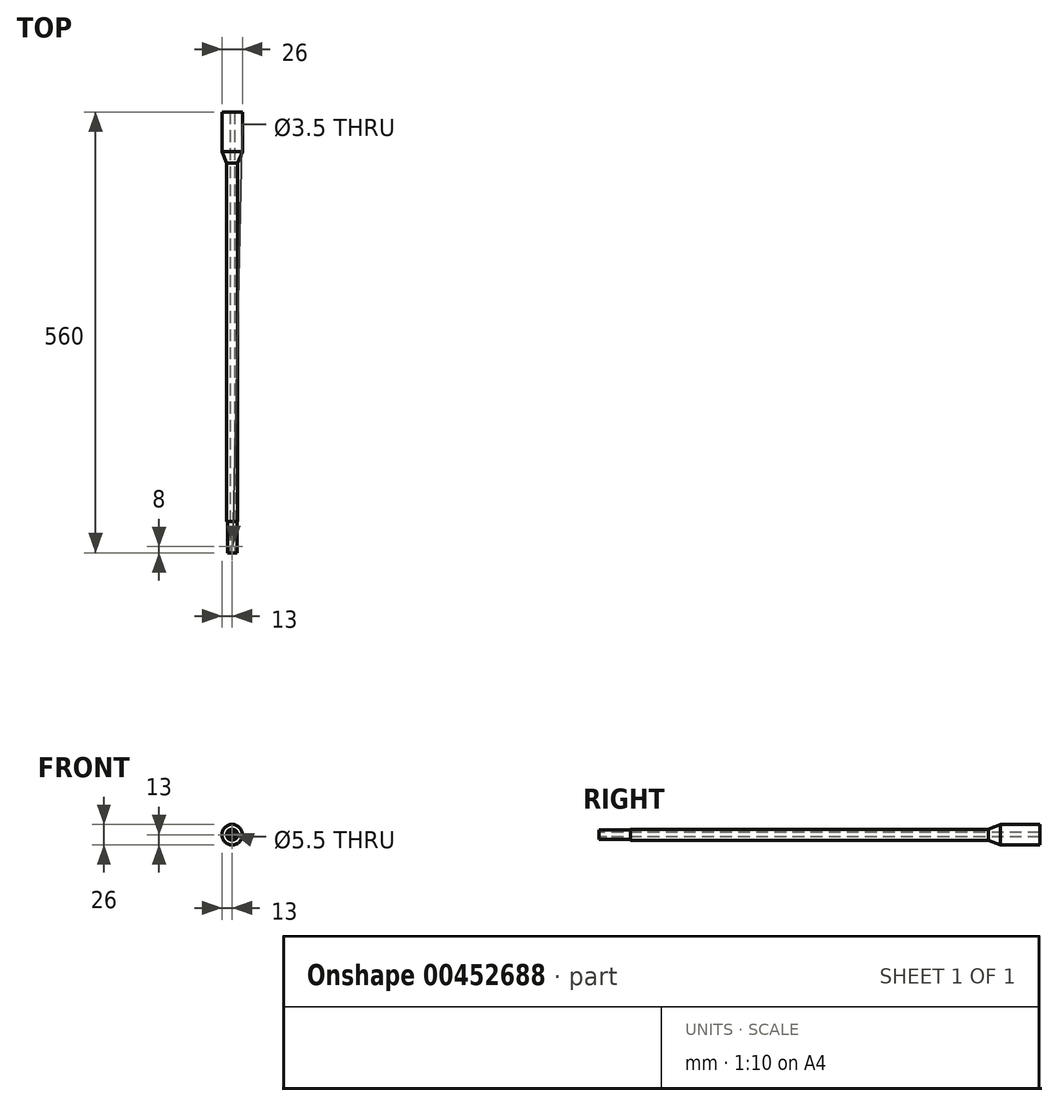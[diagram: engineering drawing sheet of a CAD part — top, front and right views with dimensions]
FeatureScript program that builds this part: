
annotation { "Feature Type Name" : "Feature", "Feature Type Description" : "" }
export const myFeature = defineFeature(function(context is Context, id is Id, definition is map)
    precondition{}
    {
        {
            var Q0;
            Q0=qCreatedBy(makeId("Front.planeOp"),FACE);
            var sketch = newSketch(context, id + "F0", { "sketchPlane" : qUnion([Q0])});
            skCircle(sketch, "E0", {"center": v(0, 0) * mm, "radius": 7 * mm});
            skSolve(sketch);
        }
        {
            var Q0;
            Q0=makeQuery(id+"F0.imprint","IMPRINT",FACE,{"disambiguationData":[TD([[makeQuery(id+"F0.imprint","IMPRINT",EDGE,{"derivedFrom":sQuery(id+"F0.wireOp",EDGE,"E0")}),1.0]])]});
            extrude(context, id + "F1", {"entities" : qUnion([Q0]), "oppositeDirection" : true, "depth" : 560 * mm});
        }
        {
            var Q0;
            Q0=makeQuery(id+"F1.opExtrude","CAP_FACE",FACE,{"disambiguationData":[OSD([sQuery(id+"F0.wireOp",EDGE,"E0")])],"isStart":true});
            var sketch = newSketch(context, id + "F2", { "sketchPlane" : qUnion([Q0])});
            skCircle(sketch, "E1", {"center": v(0, 0) * mm, "radius": 6 * mm});
            skSolve(sketch);
        }
        {
            var Q0;
            Q0=makeQuery(id+"F2.imprint","IMPRINT",FACE,{"disambiguationData":[TD([[makeQuery(id+"F2.imprint","IMPRINT",EDGE,{"derivedFrom":sQuery(id+"F2.wireOp",EDGE,"E1")}),-1.0]])]});
            extrude(context, id + "F3", {"entities" : qUnion([Q0]), "operationType" : NewBodyOperationType.REMOVE, "oppositeDirection" : true, "depth" : 40 * mm});
        }
        {
            var Q0;
            Q0=makeQuery(id+"F1.opExtrude","CAP_FACE",FACE,{"disambiguationData":[OSD([sQuery(id+"F0.wireOp",EDGE,"E0")])],"isStart":true});
            var sketch = newSketch(context, id + "F4", { "sketchPlane" : qUnion([Q0])});
            skCircle(sketch, "E2", {"center": v(0, 0) * mm, "radius": 2.75 * mm});
            skSolve(sketch);
        }
        {
            var Q0;
            Q0=makeQuery(id+"F4.imprint","IMPRINT",FACE,{"disambiguationData":[TD([[makeQuery(id+"F4.imprint","IMPRINT",EDGE,{"derivedFrom":sQuery(id+"F4.wireOp",EDGE,"E2")}),1.0]])]});
            extrude(context, id + "F5", {"entities" : qUnion([Q0]), "operationType" : NewBodyOperationType.REMOVE, "endBound" : BoundingType.THROUGH_ALL, "oppositeDirection" : true, "depth" : 25 * mm});
        }
        {
            var Q0;
            Q0=qCreatedBy(makeId("Top.planeOp"),FACE);
            var sketch = newSketch(context, id + "F6", { "sketchPlane" : qUnion([Q0])});
            skCircle(sketch, "E3", {"center": v(0, 8) * mm, "radius": 1.75 * mm});
            skSolve(sketch);
        }
        {
            var Q0;
            Q0 = qSketchRegion(id + "F6", true);
            extrude(context, id + "F7", {"entities" : qUnion([Q0]), "operationType" : NewBodyOperationType.REMOVE, "oppositeDirection" : true, "depth" : 10 * mm});
        }
        {
            var Q0;
            Q0=makeQuery(id+"F1.opExtrude","CAP_FACE",FACE,{"disambiguationData":[OSD([sQuery(id+"F0.wireOp",EDGE,"E0")])],"isStart":false});
            var sketch = newSketch(context, id + "F8", { "sketchPlane" : qUnion([Q0])});
            skCircle(sketch, "E4", {"center": v(0, 0) * mm, "radius": 13 * mm});
            skSolve(sketch);
        }
        {
            var Q0;
            Q0=makeQuery(id+"F8.imprint","IMPRINT",FACE,{"disambiguationData":[TD([[makeQuery(id+"F8.imprint","IMPRINT",EDGE,{"derivedFrom":sQuery(id+"F8.wireOp",EDGE,"E4")}),1.0]])]});
            extrude(context, id + "F9", {"entities" : qUnion([Q0]), "operationType" : NewBodyOperationType.ADD, "oppositeDirection" : true, "depth" : 70 * mm});
        }
        {
            var Q0;
            Q0=makeQuery(id+"F9.opExtrude","CAP_EDGE",EDGE,{"disambiguationData":[OSD([sQuery(id+"F8.wireOp",EDGE,"E4")])],"isStart":false});
            chamfer(context, id + "F10", {"entities" : qUnion([Q0]), "chamferType" : ChamferType.TWO_OFFSETS, "width1" : 20 * mm, "oppositeDirection" : false, "width2" : 8 * mm, "tangentPropagation" : true});
        }
    });
